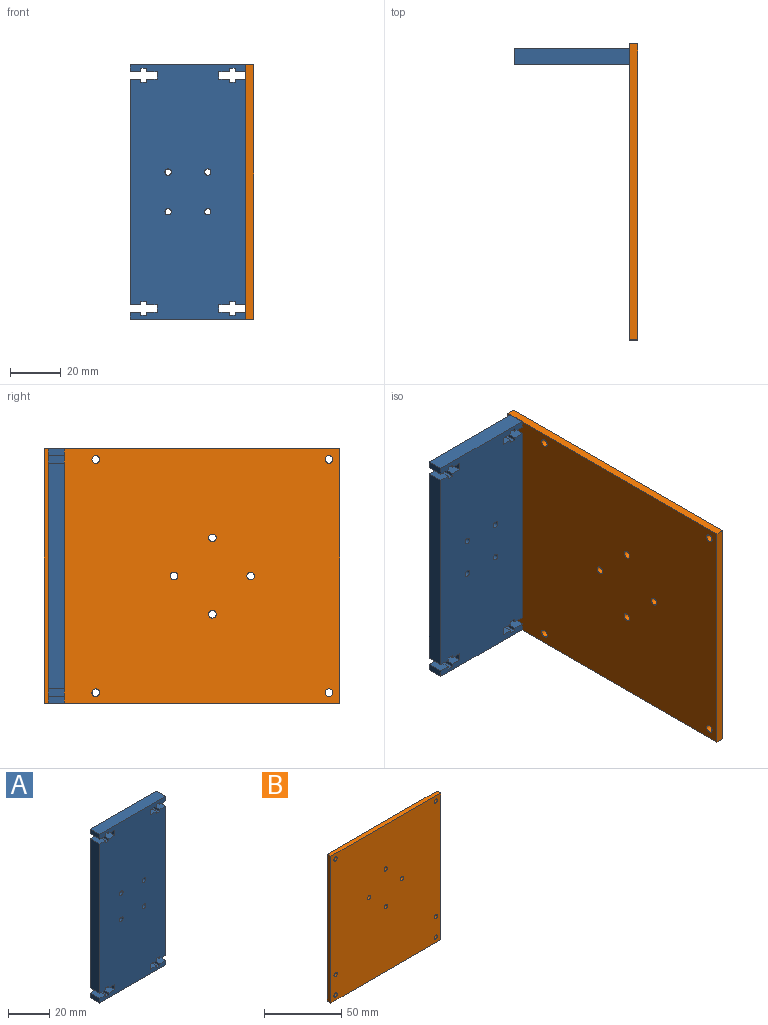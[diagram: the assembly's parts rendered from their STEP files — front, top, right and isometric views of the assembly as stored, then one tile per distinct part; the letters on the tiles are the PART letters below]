
ASSEMBLY  parts=2 mates=1
PART A: 58 faces, bbox 45.3x6.4x100 mm
  f0: plane 6.35x4.08mm, normal (0,0,1), area 25.9mm2, adj f1,f55,f56,f57
  f1: plane 6.35x1.21mm, normal (-1,0,0), area 7.7mm2, adj f0,f2,f56,f57
  f2: plane 6.35x2.34mm, normal (0,0,1), area 14.9mm2, adj f1,f3,f56,f57
  f3: plane 6.35x1.21mm, normal (1,0,0), area 7.7mm2, adj f2,f4,f56,f57
  f4: plane 6.35x4.08mm, normal (0,0,1), area 25.9mm2, adj f3,f5,f56,f57
  f5: plane 6.35x2.74mm, normal (-1,0,0), area 17.4mm2, adj f4,f6,f56,f57
  f6: plane 45.25x6.35mm, normal (0,0,-1), area 287.3mm2, adj f5,f7,f56,f57
  f7: plane 6.35x2.74mm, normal (1,0,0), area 17.4mm2, adj f6,f8,f56,f57
  f8: plane 6.35x4.08mm, normal (0,0,1), area 25.9mm2, adj f7,f9,f56,f57
  f9: plane 6.35x1.21mm, normal (-1,0,0), area 7.7mm2, adj f8,f10,f56,f57
  f10: plane 6.35x2.34mm, normal (0,0,1), area 14.9mm2, adj f9,f11,f56,f57
  f11: plane 6.35x1.21mm, normal (1,0,0), area 7.7mm2, adj f10,f12,f56,f57
  f12: plane 6.35x4.08mm, normal (0,0,1), area 25.9mm2, adj f11,f13,f56,f57
  f13: plane 6.35x3mm, normal (1,0,0), area 19.1mm2, adj f12,f14,f56,f57
  f14: plane 6.35x4.08mm, normal (0,0,-1), area 25.9mm2, adj f13,f15,f56,f57
  f15: plane 6.35x1.21mm, normal (1,0,0), area 7.7mm2, adj f14,f16,f56,f57
  f16: plane 6.35x2.34mm, normal (0,0,-1), area 14.9mm2, adj f15,f17,f56,f57
  f17: plane 6.35x1.21mm, normal (-1,0,0), area 7.7mm2, adj f16,f18,f56,f57
  f18: plane 6.35x4.08mm, normal (0,0,-1), area 25.9mm2, adj f17,f19,f56,f57
  f19: plane 88.52x6.35mm, normal (1,0,0), area 562.1mm2, adj f18,f20,f56,f57
  f20: plane 6.35x4.08mm, normal (0,0,1), area 25.9mm2, adj f19,f21,f56,f57
  f21: plane 6.35x1.21mm, normal (-1,0,0), area 7.7mm2, adj f20,f22,f56,f57
  f22: plane 6.35x2.34mm, normal (0,0,1), area 14.9mm2, adj f21,f23,f56,f57
  f23: plane 6.35x1.21mm, normal (1,0,0), area 7.7mm2, adj f22,f24,f56,f57
  f24: plane 6.35x4.08mm, normal (0,0,1), area 25.9mm2, adj f23,f25,f56,f57
  f25: plane 6.35x3mm, normal (1,0,0), area 19.1mm2, adj f24,f26,f56,f57
  f26: plane 6.35x4.08mm, normal (0,0,-1), area 25.9mm2, adj f25,f27,f56,f57
  f27: plane 6.35x1.21mm, normal (1,0,0), area 7.7mm2, adj f26,f28,f56,f57
  f28: plane 6.35x2.34mm, normal (0,0,-1), area 14.9mm2, adj f27,f29,f56,f57
  f29: plane 6.35x1.21mm, normal (-1,0,0), area 7.7mm2, adj f28,f30,f56,f57
  f30: plane 6.35x4.08mm, normal (0,0,-1), area 25.9mm2, adj f29,f31,f56,f57
  f31: plane 6.35x2.74mm, normal (1,0,0), area 17.4mm2, adj f30,f32,f56,f57
  f32: plane 45.25x6.35mm, normal (0,0,1), area 287.3mm2, adj f31,f33,f56,f57
  f33: plane 6.35x2.74mm, normal (-1,0,0), area 17.4mm2, adj f32,f34,f56,f57
  f34: plane 6.35x4.08mm, normal (0,0,-1), area 25.9mm2, adj f33,f35,f56,f57
  f35: plane 6.35x1.21mm, normal (1,0,0), area 7.7mm2, adj f34,f36,f56,f57
  f36: plane 6.35x2.34mm, normal (0,0,-1), area 14.9mm2, adj f35,f37,f56,f57
  f37: plane 6.35x1.21mm, normal (-1,0,0), area 7.7mm2, adj f36,f38,f56,f57
  f38: plane 6.35x4.08mm, normal (0,0,-1), area 25.9mm2, adj f37,f39,f56,f57
  f39: plane 6.35x3mm, normal (-1,0,0), area 19.1mm2, adj f38,f40,f56,f57
  f40: plane 6.35x4.08mm, normal (0,0,1), area 25.9mm2, adj f39,f41,f56,f57
  f41: plane 6.35x1.21mm, normal (-1,0,0), area 7.7mm2, adj f40,f42,f56,f57
  f42: plane 6.35x2.34mm, normal (0,0,1), area 14.9mm2, adj f41,f43,f56,f57
  f43: plane 6.35x1.21mm, normal (1,0,0), area 7.7mm2, adj f42,f44,f56,f57
  f44: plane 6.35x4.08mm, normal (0,0,1), area 25.9mm2, adj f43,f45,f56,f57
  f45: plane 88.52x6.35mm, normal (-1,0,0), area 562.1mm2, adj f44,f46,f56,f57
  f46: plane 6.35x4.08mm, normal (0,0,-1), area 25.9mm2, adj f45,f47,f56,f57
  f47: plane 6.35x1.21mm, normal (1,0,0), area 7.7mm2, adj f46,f48,f56,f57
  f48: plane 6.35x2.34mm, normal (0,0,-1), area 14.9mm2, adj f47,f49,f56,f57
  f49: plane 6.35x1.21mm, normal (-1,0,0), area 7.7mm2, adj f48,f50,f56,f57
  f50: plane 6.35x4.08mm, normal (0,0,-1), area 25.9mm2, adj f49,f55,f56,f57
  f51: cylinder r=1.25mm len=6.35mm, axis (0,1,0), area 49.9mm2, adj f56,f57
  f52: cylinder r=1.25mm len=6.35mm, axis (0,1,0), area 49.9mm2, adj f56,f57
  f53: cylinder r=1.25mm len=6.35mm, axis (0,1,0), area 49.9mm2, adj f56,f57
  f54: cylinder r=1.25mm len=6.35mm, axis (0,1,0), area 49.9mm2, adj f56,f57
  f55: plane 6.35x3mm, normal (-1,0,0), area 19.1mm2, adj f0,f50,f56,f57
  f56: plane 100x45.25mm, normal (0,-1,0), area 4356.8mm2, adj f0,f1,f2,f3,f4,f5,f6,f7
  f57: plane 100x45.25mm, normal (0,1,0), area 4356.8mm2, adj f0,f1,f2,f3,f4,f5,f6,f7
PART B: 16 faces, bbox 100x3.2x116 mm
  f0: plane 116x3.15mm, normal (1,0,0), area 365.4mm2, adj f1,f13,f14,f15
  f1: plane 100x3.15mm, normal (0,0,1), area 315mm2, adj f0,f2,f14,f15
  f2: plane 116x3.15mm, normal (-1,0,0), area 365.4mm2, adj f1,f13,f14,f15
  f3: cylinder r=1.5mm len=3.15mm, axis (0,1,0), area 29.7mm2, adj f14,f15
  f4: cylinder r=1.5mm len=3.15mm, axis (0,1,0), area 29.7mm2, adj f14,f15
  f5: cylinder r=1.5mm len=3.15mm, axis (0,1,0), area 29.7mm2, adj f14,f15
  f6: cylinder r=1.5mm len=3.15mm, axis (0,1,0), area 29.7mm2, adj f14,f15
  f7: cylinder r=1.5mm len=3.15mm, axis (0,1,0), area 29.7mm2, adj f14,f15
  f8: cylinder r=1.5mm len=3.15mm, axis (0,1,0), area 29.7mm2, adj f14,f15
  f9: cylinder r=1.5mm len=3.15mm, axis (0,1,0), area 29.7mm2, adj f14,f15
  f10: cylinder r=1.5mm len=3.15mm, axis (0,1,0), area 29.7mm2, adj f14,f15
  f11: cylinder r=1.5mm len=3.15mm, axis (0,1,0), area 29.7mm2, adj f14,f15
  f12: cylinder r=1.5mm len=3.15mm, axis (0,1,0), area 29.7mm2, adj f14,f15
  f13: plane 100x3.15mm, normal (0,0,-1), area 315mm2, adj f0,f2,f14,f15
  f14: plane 116x100mm, normal (0,-1,0), area 11529.3mm2, adj f0,f1,f2,f3,f4,f5,f6,f7
  f15: plane 116x100mm, normal (0,1,0), area 11529.3mm2, adj f0,f1,f2,f3,f4,f5,f6,f7
PLACE A t=(35.46,8.2,23.95)mm
PLACE B rot(axis=(0.58,0.58,-0.58),120deg) t=(61.23,-56.21,23.9)mm
MATE planar A.f19 <-> B.f14  axis (1,0,0) through (58.08,5.02,23.95)mm
